# Revit family: Shower-Bath_and_Shower_Trim-KOHLER-Coralais-K-PLS15601_1
name_source: partatom
category: Plumbing Fixtures
revit_build: Autodesk Revit 2017 (Build: 20160225_1515(x64)
units: mm (PartAtom-declared; Revit-internal decimal feet)

## family parameters
Cut with Voids When Loaded = No
Host = Face
OmniClass Number = 23.31.17.00
OmniClass Title = Showers
Part Type = Normal
Room Calculation Point = No
Round Connector Dimension = Use Diameter
Shared = No

## types (4) — shared parameters
Assembly Code = D2010700
CW Connection = No
Cold Water Inlet = Cold Water Inlet
Date Modified = 03/16/2020
Default Elevation = 42"
Drain Included = No
Finish = Kohler-Metal-CP-Polished_Chrome
Flow Rate = 0 GPM
HW Connection = Yes
Handle Clearance = 3 1/16"
Handle Height = 2 7/8"
Height = 6 1/2"
Hot Water Inlet = Hot Water Inlet
Length = 4 7/8"
Manufacturer = KOHLER Co.
Master Format 2014 = 22 42 23
Master Format 2014 Name = Residential Showers
Material = Premium Metal Construction
Panel Thickness = 0"
Pressure = 0.00 psi
Product Documentation Link = https://www.us.kohler.com
Product Name = Coralais
Product Page URL = http://www.us.kohler.com
Spout Reach = 4 7/8"
Tempered Water Inlet1 = Tempered Water Inlet1
Tempered Water Inlet2 = Tempered Water Inlet2
URL = https://www.us.kohler.com
Vent Connection = No
Waste Connection = No
Waste Water Outlet = Waste Water Outlet
WaterSense Certified = No
Width = 6 1/2"

## per-type parameters (varying)
| type | ADA Compliant | Description | Indexing | Model | Spout Connector Diameter | Type |
| 1/2" NPT Spout, CP-Polished Chrome | No | Bath and shower valve trim with lever handle and NPT spout, less showerhead, project pack | No | K-PLS15601-4 | 1/2" | 1 |
| 5/8" Slip-Fit Spout, CP-Polished Chrome | No | Bath and shower valve trim with lever handle and slip-fit spout, less showerhead, project pack | No | K-PLS15601-4S | 5/8" | 2 |
| 1/2" NPT Spout, Red/Blue Indexing, CP-Polished Chrome | Yes | Bath and shower valve trim with lever handle, red/blue indexing and NPT spout, less showerhead, project pack | Yes | K-PLS15601-X4 | 1/2" | 3 |
| 5/8" Slip-Fit Spout, Red/Blue Indexing, CP-Polished Chrome | No | bath and shower valve trim with lever handle, red/blue indexing and slip-fit spout, less showerhead, project pack | Yes | K-PLS15601-X4S | 5/8" | 4 |

## geometry (parser evidence)
native form markers: Sweep x11
no freeform markers — native parametric forms only
